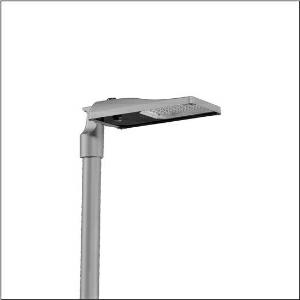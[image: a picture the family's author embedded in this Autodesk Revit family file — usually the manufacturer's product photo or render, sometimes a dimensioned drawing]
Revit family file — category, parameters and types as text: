
# Revit family: streetlight_sl_31_mini___st1_0a_5xh2d71t08ja_f6e8
name_source: partatom
category: Lighting Fixtures
units: mm (PartAtom-declared; Revit-internal decimal feet)

## family parameters
Cut with Voids When Loaded = No
Host = Face
Light Source = No
Part Type = Normal
Room Calculation Point = No
Round Connector Dimension = Use Diameter
Shared = No

## types (1)
- --- (1 x LED, 9900 lm, 82.5 W, 2200K)
    Apparent Load = 83 VA
    CIE Flux Codes = 40 73 97 100 100
    Color Rendering = 70
    Color Temperature = 2200K
    Default Elevation = 1800 mm
    Description = Streetlight SL 31 mini D4i, Desk-Remote mast luminaire for post-top, side-entry; light control with lens of PMMA; light distribution: ST1.0a, direct asymmetric distribution, for standard-compliant lighting for roads and squares; LED: luminous flux: 9.900lm, light colour: 722, colour temperature: 2200K; luminous efficacy: 120lm/W; control: pre-setting: logarithmic dimming characteristic, flexible luminous flux parameterisation, time-dependent luminous flux control, constant luminous flux control, power reduction, intelligent temperature release in ECG and LED module, overheat protection; luminaire housing, of diecast aluminium, SITECO metallic grey (DB 702S), corrosivity category C5 high according to DIN EN ISO 12944; cover of toughened safety glass, transparent, mast flange of diecast aluminium, SITECO metallic grey (DB 702S), spigot size: 76/60mm, mast flange included unmounted; cable length: 10,5m, connection cable pre-assembled; mains connection: 220..240V, AC, 50/60Hz; power consumption (at start of service life): 82,5W / (at end of service life): 90,1W / (with reduced operation 50%): 36,5W; protection rating (complete): IP66; insulation class (complete): insulation class II (safety insulation); impact resistance: IK09; certification: CE, ENEC, ENEC+, VDE, UKCA, ZD4i; permissible operating ambient temperature for outdoor applications: -40..+50°C; packaging unit: 1 piece

Light Distribution: ST1.0a
    Height = 76 mm
    Lamp = 1 x LED
    Lamp Light Flux = 9900 lm
    Lamp Power = 82.5 W
    Lamp count = 1
    Length = 547 mm
    Luminous efficacy = 120 lm/W
    Manufacturer = Siteco
    ModVariant = No
    Model = 5XH2D71T08JA
    Number of Poles = 1
    OnlyDefault = Yes
    Power Factor = 1
    Product Name = Streetlight SL 31 mini | ST1.0a
    Product group = mast luminaire | pylon top
    ProductGroupID = 6100
    Protection Class = Protection class II
    Protection Degree = IP 66
    RLX_Detail_Level = 1
    RLX_Emergency_Light_Flux = 0 lm
    RLX_Emergency_Type = 0
    RLX_Emergency_Type_DB = No
    RlxData = <blob elided: 39769 chars, md5=0b370c59>
    Socket = socket
    Standby Power = 0 W
    System Light Flux = 9900 lm
    System Power = 83 W
    Type Comments = factory setting: luminous flux: 100 % | dim-lin: 254 | 870 mA
    Type Image = l_1300332.jpg
    URL = http://relux.com
    VarID = @adj_009203
    Voltage = 0 V
    Weight = 0.00 kg
    Width = 265 mm

## geometry (parser evidence)
native form markers: Blend x4, Sweep x10
no freeform markers — native parametric forms only
